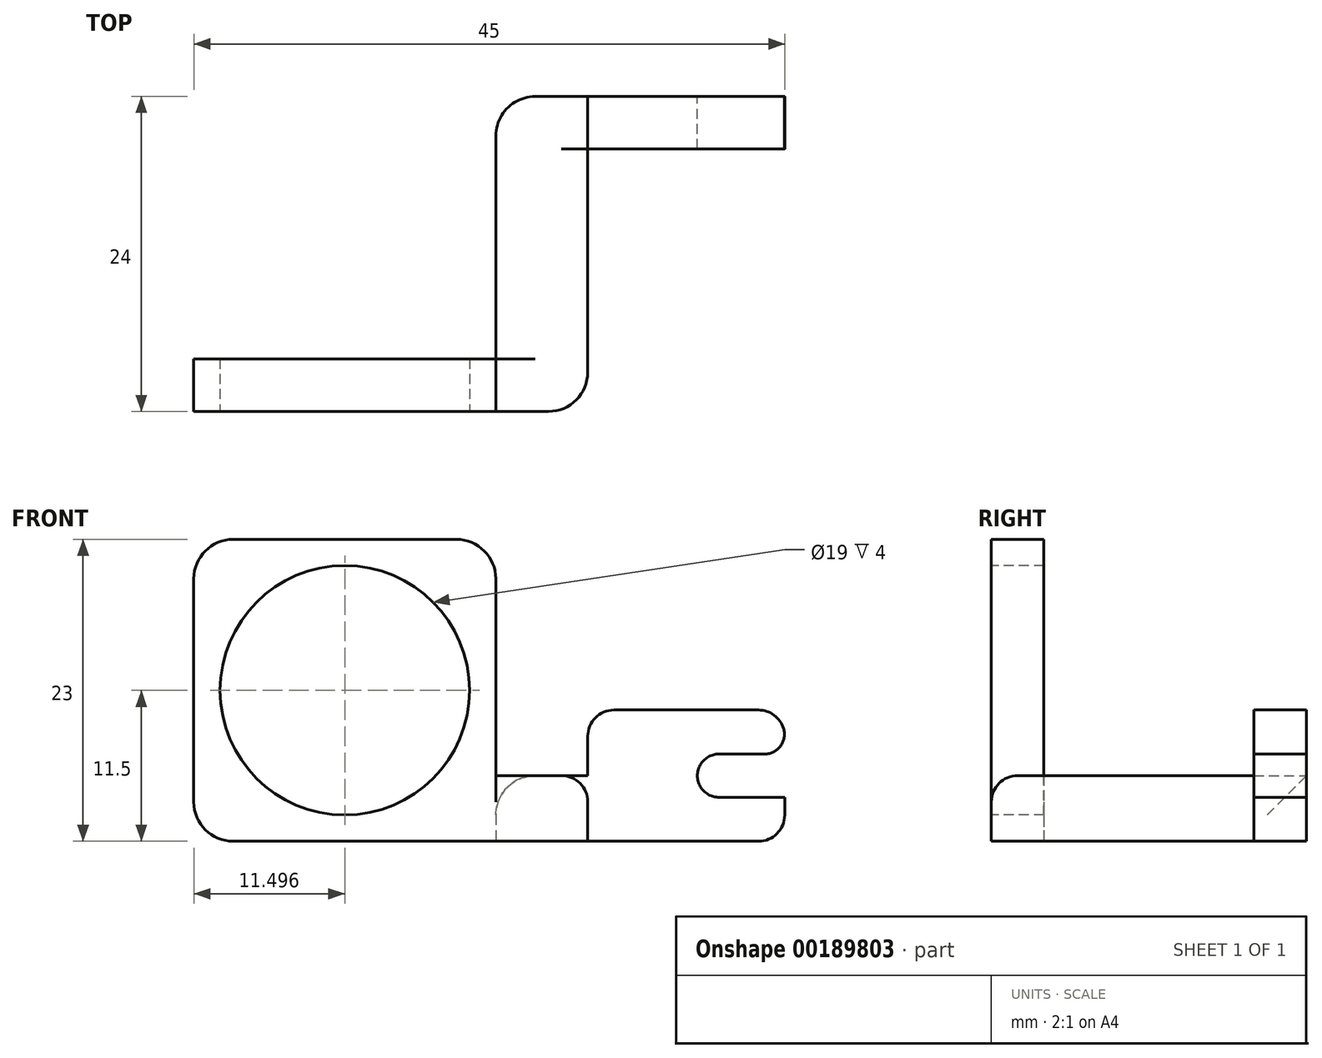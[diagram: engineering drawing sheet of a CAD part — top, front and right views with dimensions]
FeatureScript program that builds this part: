
annotation { "Feature Type Name" : "Feature", "Feature Type Description" : "" }
export const myFeature = defineFeature(function(context is Context, id is Id, definition is map)
    precondition{}
    {
        {
            var Q0;
            Q0=qCreatedBy(makeId("Top.planeOp"),FACE);
            var sketch = newSketch(context, id + "F0", { "sketchPlane" : qUnion([Q0])});
            skLineSegment(sketch, "E0.bottom", {"start": v(-15.8, -8.6) * mm, "end": v(-0.8, -8.6) * mm});
            skLineSegment(sketch, "E0.top", {"start": v(-15.8, -12.6) * mm, "end": v(-0.8, -12.6) * mm});
            skLineSegment(sketch, "E0.left", {"start": v(-15.8, -8.6) * mm, "end": v(-15.8, -12.6) * mm});
            skLineSegment(sketch, "E0.right", {"start": v(-0.8, -8.6) * mm, "end": v(-0.8, -12.6) * mm});
            skLineSegment(sketch, "E1", {"start": v(-15.8, -8.6) * mm, "end": v(-22.8, -8.6) * mm});
            skLineSegment(sketch, "E2", {"start": v(-22.8, -8.6) * mm, "end": v(-22.8, -28.6) * mm});
            skLineSegment(sketch, "E3", {"start": v(-22.8, -28.6) * mm, "end": v(-45.8, -28.6) * mm});
            skLineSegment(sketch, "E4", {"start": v(-45.8, -28.6) * mm, "end": v(-45.8, -32.6) * mm});
            skLineSegment(sketch, "E5", {"start": v(-45.8, -32.6) * mm, "end": v(-15.8, -32.6) * mm});
            skLineSegment(sketch, "E6", {"start": v(-15.8, -32.6) * mm, "end": v(-15.8, -12.6) * mm});
            skLineSegment(sketch, "E7", {"start": v(-22.8, -28.6) * mm, "end": v(-22.8, -32.6) * mm});
            skSolve(sketch);
        }
        {
            var Q0;
            Q0=makeQuery(id+"F0.imprint","IMPRINT",FACE,{"disambiguationData":[TD([[makeQuery(id+"F0.imprint","IMPRINT",EDGE,{"derivedFrom":sQuery(id+"F0.wireOp",EDGE,"E0.left")}),-1.0]])]});
            extrude(context, id + "F1", {"entities" : qUnion([Q0]), "depth" : 5 * mm});
        }
        {
            var Q0;
            Q0=makeQuery(id+"F0.imprint","IMPRINT",FACE,{"disambiguationData":[TD([[makeQuery(id+"F0.imprint","IMPRINT",EDGE,{"derivedFrom":sQuery(id+"F0.wireOp",EDGE,"E3")}),1.0]])]});
            extrude(context, id + "F2", {"entities" : qUnion([Q0]), "operationType" : NewBodyOperationType.ADD, "depth" : 23 * mm});
        }
        {
            var Q0;
            {var subQ0=sQuery(id+"F0.wireOp",EDGE,"E5");Q0=makeQuery(id+"F2.boolean.opBoolean","MERGE",FACE,{"derivedFrom":[makeQuery(id+"F1.opExtrude","SWEPT_FACE",FACE,{"disambiguationData":[OSD([subQ0])]}),makeQuery(id+"F2.opExtrude","SWEPT_FACE",FACE,{"disambiguationData":[OSD([subQ0])]})]});}
            var sketch = newSketch(context, id + "F3", { "sketchPlane" : qUnion([Q0])});
            skCircle(sketch, "E8", {"center": v(-34.3, 11.5) * mm, "radius": 9.5 * mm});
            skPoint(sketch, "E8.centerSnap0", {"position": v(-45.8, 11.5) * mm});
            skPoint(sketch, "E8.centerSnap1", {"position": v(-34.3, 23) * mm});
            skSolve(sketch);
        }
        {
            var Q0;
            {var subQ0=sQuery(id+"F0.wireOp",EDGE,"E5");var subQ1=sQuery(id+"F0.wireOp",EDGE,"E7");var subQ2=sQuery(id+"F0.wireOp",EDGE,"E2");Q0=makeQuery(id+"F2.boolean.opBoolean","SPLIT",EDGE,{"disambiguationData":[TD([makeQuery(id+"F1.opExtrude","SWEPT_FACE",FACE,{"disambiguationData":[OSD([subQ0])]})])],"derivedFrom":makeQuery(id+"F1.opExtrude","CAP_EDGE",EDGE,{"disambiguationData":[OSD([subQ2,subQ1])],"isStart":false})});}
            var Q1;
            Q1=makeQuery(id+"F2.opExtrude","CAP_EDGE",EDGE,{"disambiguationData":[OSD([sQuery(id+"F0.wireOp",EDGE,"E7")])],"isStart":false});
            var Q2;
            Q2=makeQuery(id+"F2.opExtrude","CAP_EDGE",EDGE,{"disambiguationData":[OSD([sQuery(id+"F0.wireOp",EDGE,"E4")])],"isStart":false});
            var Q3;
            Q3=makeQuery(id+"F2.opExtrude","CAP_EDGE",EDGE,{"disambiguationData":[OSD([sQuery(id+"F0.wireOp",EDGE,"E4")])],"isStart":true});
            var Q4;
            Q4=makeQuery(id+"F1.opExtrude","SWEPT_EDGE",EDGE,{"disambiguationData":[OSD([sQuery(id+"F0.wireOp",EDGE,"E0.top"),sQuery(id+"F0.wireOp",EDGE,"E0.left"),sQuery(id+"F0.wireOp",EDGE,"E6")])]});
            var Q5;
            Q5=makeQuery(id+"F1.opExtrude","SWEPT_EDGE",EDGE,{"disambiguationData":[OSD([sQuery(id+"F0.wireOp",EDGE,"E1"),sQuery(id+"F0.wireOp",EDGE,"E2")])]});
            var Q6;
            Q6=makeQuery(id+"F1.opExtrude","SWEPT_EDGE",EDGE,{"disambiguationData":[OSD([sQuery(id+"F0.wireOp",EDGE,"E5"),sQuery(id+"F0.wireOp",EDGE,"E6")])]});
            fillet(context, id + "F4", {"entities" : qUnion([Q0, Q1, Q2, Q3, Q4, Q5, Q6]), "radius" : 3 * mm, "tangentPropagation" : true, "allowEdgeOverflow" : false});
        }
        {
            var Q0;
            Q0=makeQuery(id+"F3.imprint","IMPRINT",FACE,{"disambiguationData":[TD([[makeQuery(id+"F3.imprint","IMPRINT",EDGE,{"derivedFrom":sQuery(id+"F3.wireOp",EDGE,"E8")}),1.0]])]});
            extrude(context, id + "F5", {"entities" : qUnion([Q0]), "operationType" : NewBodyOperationType.REMOVE, "oppositeDirection" : true, "depth" : 25 * mm});
        }
        {
            var Q0;
            Q0=makeQuery(id+"F0.imprint","IMPRINT",FACE,{"disambiguationData":[TD([[makeQuery(id+"F0.imprint","IMPRINT",EDGE,{"derivedFrom":sQuery(id+"F0.wireOp",EDGE,"E0.bottom")}),-1.0]])]});
            extrude(context, id + "F6", {"entities" : qUnion([Q0]), "operationType" : NewBodyOperationType.ADD, "depth" : 10 * mm});
        }
        {
            var Q0;
            {var subQ0=sQuery(id+"F0.wireOp",EDGE,"E1");var subQ1=sQuery(id+"F0.wireOp",EDGE,"E6");var subQ2=sQuery(id+"F0.wireOp",EDGE,"E0.left");Q0=makeQuery(id+"F6.boolean.opBoolean","SPLIT",EDGE,{"disambiguationData":[TD([makeQuery(id+"F1.opExtrude","SWEPT_FACE",FACE,{"disambiguationData":[OSD([subQ0])]})])],"derivedFrom":makeQuery(id+"F1.opExtrude","CAP_EDGE",EDGE,{"disambiguationData":[OSD([subQ2,subQ1])],"isStart":false})});}
            var Q1;
            Q1=makeQuery(id+"F6.opExtrude","CAP_EDGE",EDGE,{"disambiguationData":[OSD([sQuery(id+"F0.wireOp",EDGE,"E0.left")])],"isStart":false});
            var Q2;
            Q2=makeQuery(id+"F6.opExtrude","CAP_EDGE",EDGE,{"disambiguationData":[OSD([sQuery(id+"F0.wireOp",EDGE,"E0.right")])],"isStart":false});
            var Q3;
            Q3=makeQuery(id+"F6.opExtrude","CAP_EDGE",EDGE,{"disambiguationData":[OSD([sQuery(id+"F0.wireOp",EDGE,"E0.right")])],"isStart":true});
            fillet(context, id + "F7", {"entities" : qUnion([Q0, Q1, Q2, Q3]), "radius" : 2 * mm, "tangentPropagation" : true, "allowEdgeOverflow" : false});
        }
        {
            var Q0;
            Q0=makeQuery(id+"F6.boolean.opBoolean","MERGE",FACE,{"derivedFrom":[makeQuery(id+"F1.opExtrude","SWEPT_FACE",FACE,{"disambiguationData":[OSD([sQuery(id+"F0.wireOp",EDGE,"E1")])]}),makeQuery(id+"F6.opExtrude","SWEPT_FACE",FACE,{"disambiguationData":[OSD([sQuery(id+"F0.wireOp",EDGE,"E0.bottom")])]})]});
            var sketch = newSketch(context, id + "F8", { "sketchPlane" : qUnion([Q0])});
            skCircle(sketch, "E9", {"center": v(5.8, 5) * mm, "radius": 1.65 * mm});
            skPoint(sketch, "E9.centerSnap0", {"position": v(8.3, 10) * mm});
            skPoint(sketch, "E9.centerSnap1", {"position": v(0.8, 5) * mm});
            skLineSegment(sketch, "E10", {"start": v(5.8, 6.65) * mm, "end": v(0.8, 6.65) * mm});
            skLineSegment(sketch, "E11", {"start": v(5.8, 3.35) * mm, "end": v(0.8, 3.35) * mm});
            skSolve(sketch);
        }
        {
            var Q0;
            Q0=makeQuery(id+"F8.imprint","IMPRINT",FACE,{"disambiguationData":[TD([[makeQuery(id+"F8.imprint","IMPRINT",EDGE,{"derivedFrom":sQuery(id+"F8.wireOp",EDGE,"E9")}),1.0]])]});
            extrude(context, id + "F9", {"entities" : qUnion([Q0]), "operationType" : NewBodyOperationType.REMOVE, "oppositeDirection" : true, "depth" : 25 * mm});
        }
        {
            var Q0;
            {var subQ0=sQuery(id+"F8.wireOp",EDGE,"E10");Q0=makeQuery(id+"F8.imprint","IMPRINT",FACE,{"disambiguationData":[TD([[makeQuery(id+"F8.imprint","IMPRINT",EDGE,{"derivedFrom":subQ0}),1.0]])]});}
            extrude(context, id + "F10", {"entities" : qUnion([Q0]), "operationType" : NewBodyOperationType.REMOVE, "oppositeDirection" : true, "depth" : 25 * mm});
        }
        {
            var Q0;
            Q0=makeQuery(id+"F10.boolean.opBoolean","COPY",EDGE,{"derivedFrom":makeQuery(id+"F10.opExtrude","SWEPT_EDGE",EDGE,{"disambiguationData":[OSD([sQuery(id+"F0.wireOp",EDGE,"E0.bottom"),sQuery(id+"F0.wireOp",EDGE,"E0.right"),sQuery(id+"F8.wireOp",EDGE,"E11")])]})});
            var Q1;
            Q1=makeQuery(id+"F10.boolean.opBoolean","COPY",EDGE,{"derivedFrom":makeQuery(id+"F10.opExtrude","SWEPT_EDGE",EDGE,{"disambiguationData":[OSD([sQuery(id+"F0.wireOp",EDGE,"E0.bottom"),sQuery(id+"F0.wireOp",EDGE,"E0.right"),sQuery(id+"F8.wireOp",EDGE,"E10")])]})});
            fillet(context, id + "F11", {"entities" : qUnion([Q0, Q1]), "radius" : 1.5 * mm, "tangentPropagation" : true, "allowEdgeOverflow" : false});
        }
    });
